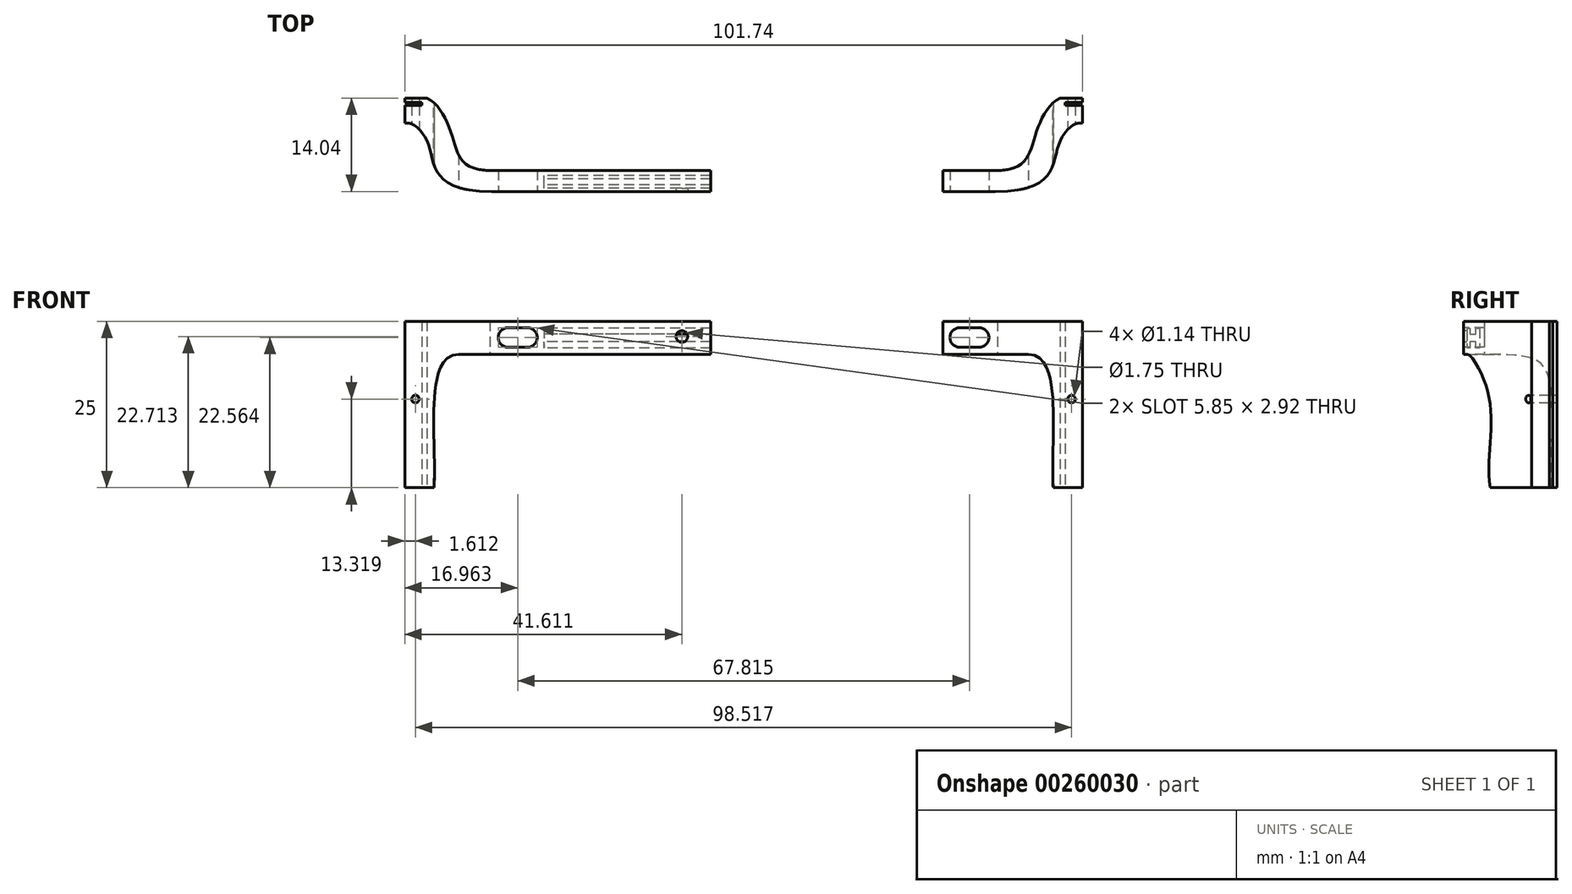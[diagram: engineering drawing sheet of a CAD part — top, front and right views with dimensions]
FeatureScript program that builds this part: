
annotation { "Feature Type Name" : "Feature", "Feature Type Description" : "" }
export const myFeature = defineFeature(function(context is Context, id is Id, definition is map)
    precondition{}
    {
        {
            var Q0;
            Q0=qCreatedBy(makeId("Top.planeOp"),FACE);
            var sketch = newSketch(context, id + "F0", { "sketchPlane" : qUnion([Q0])});
            skLineSegment(sketch, "E0.bottom", {"start": v(47.55, 5.5) * mm, "end": v(50.87, 5.5) * mm});
            skLineSegment(sketch, "E0.top", {"start": v(29.93, -8.54) * mm, "end": v(37.83, -8.54) * mm});
            skLineSegment(sketch, "E0.right", {"start": v(50.87, 5.5) * mm, "end": v(50.87, 4.86) * mm});
            skLineSegment(sketch, "E1", {"start": v(29.93, -5.39) * mm, "end": v(38.1, -5.39) * mm});
            skFitSpline(sketch, "E2", {"points": [v(38.1, -5.39) * mm, v(43.83, 0) * mm, v(50.87, 5.5) * mm], "startDerivative": vector(28.4, 0.4) * mm, "endDerivative": vector(24.05, -8.74) * mm});
            skFitSpline(sketch, "E3", {"points": [v(37.83, -8.54) * mm, v(47.31, -1.52) * mm, v(50.87, 1.72) * mm], "startDerivative": vector(45.04, 0) * mm, "endDerivative": vector(11.01, -1.93) * mm});
            skLineSegment(sketch, "E4.bottom", {"start": v(50.87, 4.86) * mm, "end": v(48.29, 4.86) * mm});
            skLineSegment(sketch, "E4.top", {"start": v(50.87, 4.37) * mm, "end": v(48.29, 4.37) * mm});
            skLineSegment(sketch, "E4.right", {"start": v(48.29, 4.86) * mm, "end": v(48.29, 4.37) * mm});
            skLineSegment(sketch, "E5.trimOffspring", {"start": v(50.87, 4.37) * mm, "end": v(50.87, 1.72) * mm});
            skLineSegment(sketch, "E6", {"start": v(29.93, -5.39) * mm, "end": v(29.93, -8.54) * mm});
            skSolve(sketch);
        }
        {
            var Q0;
            Q0=makeQuery(id+"F0.imprint","IMPRINT",FACE,{"disambiguationData":[TD([[makeQuery(id+"F0.imprint","IMPRINT",EDGE,{"derivedFrom":sQuery(id+"F0.wireOp",EDGE,"E0.bottom")}),-1.0]])]});
            extrude(context, id + "F1", {"entities" : qUnion([Q0]), "depth" : 25 * mm});
        }
        {
            var Q0;
            Q0=makeQuery(id+"F1.opExtrude","SWEPT_FACE",FACE,{"disambiguationData":[OSD([sQuery(id+"F0.wireOp",EDGE,"E0.top")])]});
            var sketch = newSketch(context, id + "F2", { "sketchPlane" : qUnion([Q0])});
            skLineSegment(sketch, "E7", {"start": v(29.93, 20.02) * mm, "end": v(42.77, 20.02) * mm});
            skFitSpline(sketch, "E8", {"points": [v(42.77, 20.02) * mm, v(46.48, 0) * mm], "startDerivative": vector(16.13, 0.2) * mm, "endDerivative": vector(1.4, -21.42) * mm});
            skLineSegment(sketch, "E9", {"start": v(29.93, 20.02) * mm, "end": v(29.93, 0) * mm});
            skLineSegment(sketch, "E10", {"start": v(29.93, 0) * mm, "end": v(46.48, 0) * mm});
            skArc(sketch, "E11", {"start": v(32.45, 24.03) * mm, "mid": v(30.98, 22.56) * mm, "end": v(32.45, 21.1) * mm});
            skArc(sketch, "E12", {"start": v(35.37, 21.1) * mm, "mid": v(36.83, 22.56) * mm, "end": v(35.37, 24.03) * mm});
            skLineSegment(sketch, "E13", {"start": v(32.45, 24.03) * mm, "end": v(35.37, 24.03) * mm});
            skLineSegment(sketch, "E14", {"start": v(35.37, 21.1) * mm, "end": v(32.45, 21.1) * mm});
            skPoint(sketch, "E15.center.orphan", {"position": v(33.9, 22.56) * mm});
            skCircle(sketch, "E16", {"center": v(49.26, 13.32) * mm, "radius": 0.57 * mm});
            skSolve(sketch);
        }
        {
            var Q0;
            Q0=qSketchRegion(id+"F2",true);
            extrude(context, id + "F3", {"entities" : qUnion([Q0]), "operationType" : NewBodyOperationType.REMOVE, "oppositeDirection" : true, "depth" : 25 * mm});
        }
        {
            var Q0;
            Q0=makeQuery(id+"F1.opExtrude","SWEPT_BODY",BODY,{"disambiguationData":[OSD([sQuery(id+"F0.wireOp",EDGE,"E0.bottom"),sQuery(id+"F0.wireOp",EDGE,"E0.top"),sQuery(id+"F0.wireOp",EDGE,"E0.right"),sQuery(id+"F0.wireOp",EDGE,"E1"),sQuery(id+"F0.wireOp",EDGE,"E2"),sQuery(id+"F0.wireOp",EDGE,"E3"),sQuery(id+"F0.wireOp",EDGE,"E4.bottom"),sQuery(id+"F0.wireOp",EDGE,"E4.top"),sQuery(id+"F0.wireOp",EDGE,"E4.right"),sQuery(id+"F0.wireOp",EDGE,"E5.trimOffspring"),sQuery(id+"F0.wireOp",EDGE,"E6")])]});
            var Q1;
            Q1=qCreatedBy(makeId("Right.planeOp"),FACE);
            mirror(context, id + "F4", {"entities" : qUnion([Q0]), "mirrorPlane" : qUnion([Q1])});
        }
        {
            var Q0;
            Q0=makeQuery(id+"F4.opPattern","COPY",FACE,{"derivedFrom":makeQuery(id+"F1.opExtrude","SWEPT_FACE",FACE,{"disambiguationData":[OSD([sQuery(id+"F0.wireOp",EDGE,"E6")])]}),"instanceName":"1"});
            var sketch = newSketch(context, id + "F5", { "sketchPlane" : qUnion([Q0])});
            skLineSegment(sketch, "E17", {"start": v(-8.03, 23.95) * mm, "end": v(-8.03, 21) * mm});
            skLineSegment(sketch, "E18", {"start": v(-8.03, 23.95) * mm, "end": v(-7.57, 23.95) * mm});
            skLineSegment(sketch, "E19", {"start": v(-7.57, 23.95) * mm, "end": v(-7.57, 23.06) * mm});
            skLineSegment(sketch, "E20", {"start": v(-7.57, 23.06) * mm, "end": v(-6.64, 23.06) * mm});
            skLineSegment(sketch, "E21", {"start": v(-6.64, 23.06) * mm, "end": v(-6.64, 23.95) * mm});
            skLineSegment(sketch, "E22", {"start": v(-6.64, 23.95) * mm, "end": v(-6.13, 23.95) * mm});
            skLineSegment(sketch, "E23", {"start": v(-6.13, 23.95) * mm, "end": v(-6.13, 21) * mm});
            skLineSegment(sketch, "E24", {"start": v(-6.13, 21) * mm, "end": v(-6.64, 21) * mm});
            skLineSegment(sketch, "E25", {"start": v(-6.64, 21) * mm, "end": v(-6.64, 21.92) * mm});
            skLineSegment(sketch, "E26", {"start": v(-6.64, 21.92) * mm, "end": v(-7.57, 21.92) * mm});
            skLineSegment(sketch, "E27", {"start": v(-7.57, 21.92) * mm, "end": v(-7.57, 21) * mm});
            skLineSegment(sketch, "E28", {"start": v(-7.57, 21) * mm, "end": v(-8.03, 21) * mm});
            skLineSegment(sketch, "E29.bottom", {"start": v(-8.54, 25) * mm, "end": v(-5.39, 25) * mm});
            skLineSegment(sketch, "E29.top", {"start": v(-8.54, 20.02) * mm, "end": v(-5.39, 20.02) * mm});
            skLineSegment(sketch, "E29.left", {"start": v(-8.54, 25) * mm, "end": v(-8.54, 20.02) * mm});
            skLineSegment(sketch, "E29.right", {"start": v(-5.39, 25) * mm, "end": v(-5.39, 20.02) * mm});
            skSolve(sketch);
        }
        {
            var Q0;
            Q0 = qSketchRegion(id + "F5", true);
            extrude(context, id + "F6", {"entities" : qUnion([Q0]), "operationType" : NewBodyOperationType.ADD, "depth" : 25 * mm});
        }
        {
            var Q0;
            Q0=makeQuery(id+"F6.boolean.opBoolean","MERGE",FACE,{"derivedFrom":[makeQuery(id+"F4.opPattern","COPY",FACE,{"derivedFrom":makeQuery(id+"F1.opExtrude","SWEPT_FACE",FACE,{"disambiguationData":[OSD([sQuery(id+"F0.wireOp",EDGE,"E0.top")])]}),"instanceName":"1"}),makeQuery(id+"F6.opExtrude","SWEPT_FACE",FACE,{"disambiguationData":[OSD([sQuery(id+"F5.wireOp",EDGE,"E29.left")])]})]});
            var sketch = newSketch(context, id + "F7", { "sketchPlane" : qUnion([Q0])});
            skCircle(sketch, "E30", {"center": v(-9.26, 22.71) * mm, "radius": 0.87 * mm});
            skSolve(sketch);
        }
        {
            var Q0;
            Q0 = qSketchRegion(id + "F7", true);
            extrude(context, id + "F8", {"entities" : qUnion([Q0]), "operationType" : NewBodyOperationType.REMOVE, "endBound" : BoundingType.UP_TO_NEXT, "oppositeDirection" : true, "depth" : 25 * mm});
        }
    });
